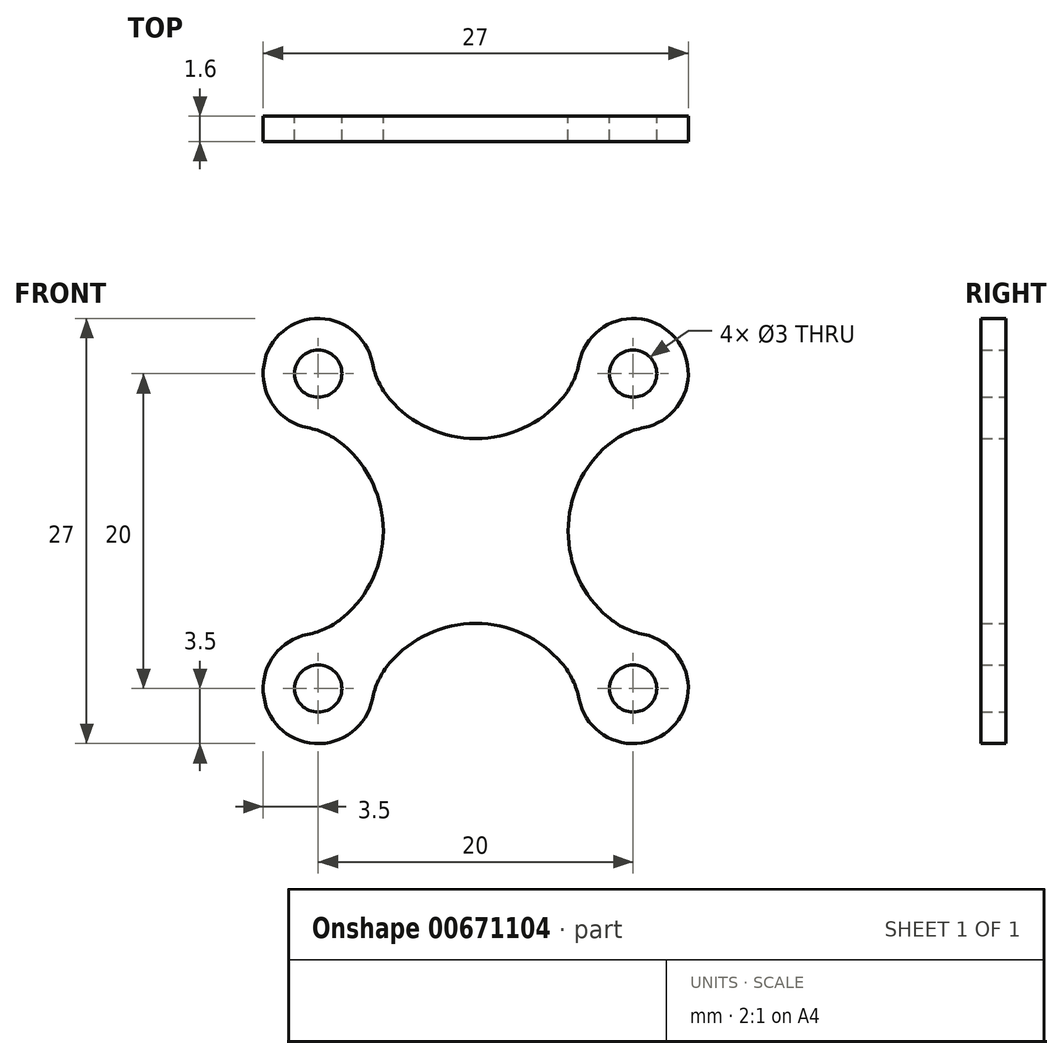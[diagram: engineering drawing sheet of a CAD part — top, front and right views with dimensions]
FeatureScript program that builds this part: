
annotation { "Feature Type Name" : "Feature", "Feature Type Description" : "" }
export const myFeature = defineFeature(function(context is Context, id is Id, definition is map)
    precondition{}
    {
        {
            var Q0;
            Q0=qCreatedBy(makeId("Front.planeOp"),FACE);
            var sketch = newSketch(context, id + "F0", { "sketchPlane" : qUnion([Q0])});
            skPoint(sketch, "E0.middle", {"position": v(0, 0) * mm});
            skCircle(sketch, "E1", {"center": v(-10, 10) * mm, "radius": 1.5 * mm});
            skCircle(sketch, "E2", {"center": v(10, 10) * mm, "radius": 1.5 * mm});
            skCircle(sketch, "E3", {"center": v(10, -10) * mm, "radius": 1.5 * mm});
            skCircle(sketch, "E4", {"center": v(-10, -10) * mm, "radius": 1.5 * mm});
            skArc(sketch, "E5.0", {"start": v(-10.67, -6.57) * mm, "mid": v(-12.47, -12.47) * mm, "end": v(-6.57, -10.67) * mm});
            skArc(sketch, "E6.0", {"start": v(-6.57, 10.67) * mm, "mid": v(-12.47, 12.47) * mm, "end": v(-10.67, 6.57) * mm});
            skArc(sketch, "E7.0", {"start": v(6.57, -10.67) * mm, "mid": v(12.47, -12.47) * mm, "end": v(10.67, -6.57) * mm});
            skArc(sketch, "E8.0", {"start": v(10.67, 6.57) * mm, "mid": v(12.47, 12.47) * mm, "end": v(6.57, 10.67) * mm});
            skArc(sketch, "E9", {"start": v(5.46, -8.4) * mm, "mid": v(0, -5.87) * mm, "end": v(-5.46, -8.4) * mm});
            skArc(sketch, "E10.MirrorCS", {"start": v(-8.4, 5.46) * mm, "mid": v(-5.87, 0) * mm, "end": v(-8.4, -5.46) * mm});
            skArc(sketch, "E11.MirrorCS", {"start": v(-5.46, 8.4) * mm, "mid": v(0, 5.87) * mm, "end": v(5.46, 8.4) * mm});
            skArc(sketch, "E12.MirrorCS", {"start": v(8.4, -5.46) * mm, "mid": v(5.87, 0) * mm, "end": v(8.4, 5.46) * mm});
            skPoint(sketch, "E13.visualSharp", {"position": v(6.5, -10) * mm});
            skArc(sketch, "E13.filletArc", {"start": v(6.57, -10.67) * mm, "mid": v(6.16, -9.46) * mm, "end": v(5.46, -8.4) * mm});
            skPoint(sketch, "E14.visualSharp", {"position": v(10, -6.5) * mm});
            skArc(sketch, "E14.filletArc", {"start": v(8.4, -5.46) * mm, "mid": v(9.46, -6.16) * mm, "end": v(10.67, -6.57) * mm});
            skPoint(sketch, "E15.visualSharp", {"position": v(-6.5, -10) * mm});
            skArc(sketch, "E15.filletArc", {"start": v(-5.46, -8.4) * mm, "mid": v(-6.16, -9.46) * mm, "end": v(-6.57, -10.67) * mm});
            skPoint(sketch, "E16.visualSharp", {"position": v(-10, -6.5) * mm});
            skArc(sketch, "E16.filletArc", {"start": v(-10.67, -6.57) * mm, "mid": v(-9.46, -6.16) * mm, "end": v(-8.4, -5.46) * mm});
            skPoint(sketch, "E17.visualSharp", {"position": v(-10, 6.5) * mm});
            skArc(sketch, "E17.filletArc", {"start": v(-8.4, 5.46) * mm, "mid": v(-9.46, 6.16) * mm, "end": v(-10.67, 6.57) * mm});
            skPoint(sketch, "E18.visualSharp", {"position": v(-6.5, 10) * mm});
            skArc(sketch, "E18.filletArc", {"start": v(-6.57, 10.67) * mm, "mid": v(-6.16, 9.46) * mm, "end": v(-5.46, 8.4) * mm});
            skPoint(sketch, "E19.visualSharp", {"position": v(10, 6.5) * mm});
            skArc(sketch, "E19.filletArc", {"start": v(10.67, 6.57) * mm, "mid": v(9.46, 6.16) * mm, "end": v(8.4, 5.46) * mm});
            skPoint(sketch, "E20.visualSharp", {"position": v(6.5, 10) * mm});
            skArc(sketch, "E20.filletArc", {"start": v(5.46, 8.4) * mm, "mid": v(6.16, 9.46) * mm, "end": v(6.57, 10.67) * mm});
            skSolve(sketch);
        }
        {
            var Q0;
            Q0=makeQuery(id+"F0.imprint","IMPRINT",FACE,{"disambiguationData":[TD([[makeQuery(id+"F0.imprint","IMPRINT",EDGE,{"derivedFrom":sQuery(id+"F0.wireOp",EDGE,"E1")}),-1.0]])]});
            extrude(context, id + "F1", {"entities" : qUnion([Q0]), "depth" : 1.6 * mm, "offsetDistance" : 25 * mm});
        }
    });
